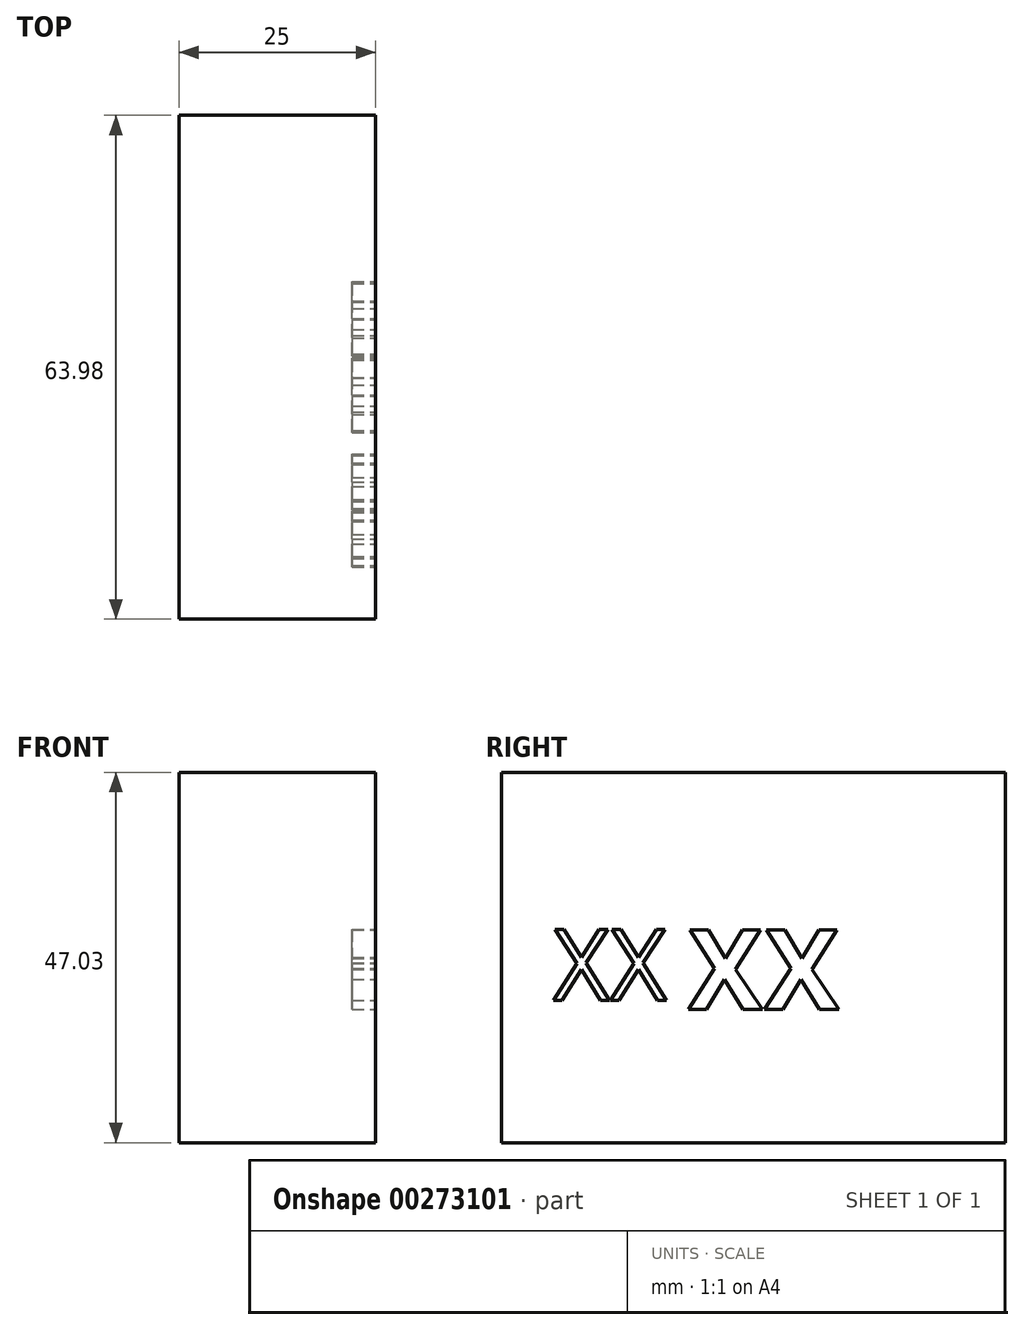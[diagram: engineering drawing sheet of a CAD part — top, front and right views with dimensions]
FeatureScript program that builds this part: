
annotation { "Feature Type Name" : "Feature", "Feature Type Description" : "" }
export const myFeature = defineFeature(function(context is Context, id is Id, definition is map)
    precondition{}
    {
        {
            var Q0;
            Q0=qCreatedBy(makeId("Right.planeOp"),FACE);
            var sketch = newSketch(context, id + "F0", { "sketchPlane" : qUnion([Q0])});
            skLineSegment(sketch, "E0.bottom", {"start": v(-63.98, 47.03) * mm, "end": v(0, 47.03) * mm});
            skLineSegment(sketch, "E0.top", {"start": v(-63.98, 0) * mm, "end": v(0, 0) * mm});
            skLineSegment(sketch, "E0.left", {"start": v(-63.98, 47.03) * mm, "end": v(-63.98, 0) * mm});
            skLineSegment(sketch, "E0.right", {"start": v(0, 47.03) * mm, "end": v(0, 0) * mm});
            skSolve(sketch);
        }
        {
            var Q0;
            Q0=makeQuery(id+"F0.imprint","IMPRINT",FACE,{"disambiguationData":[TD([[makeQuery(id+"F0.imprint","IMPRINT",EDGE,{"derivedFrom":sQuery(id+"F0.wireOp",EDGE,"E0.bottom")}),-1.0]])]});
            extrude(context, id + "F1", {"entities" : qUnion([Q0]), "depth" : 25 * mm});
        }
        {
            var Q0;
            Q0=makeQuery(id+"F1.opExtrude","CAP_FACE",FACE,{"disambiguationData":[OSD([sQuery(id+"F0.wireOp",EDGE,"E0.bottom"),sQuery(id+"F0.wireOp",EDGE,"E0.top"),sQuery(id+"F0.wireOp",EDGE,"E0.left"),sQuery(id+"F0.wireOp",EDGE,"E0.right")])],"isStart":false});
            var sketch = newSketch(context, id + "F2", { "sketchPlane" : qUnion([Q0])});
            skText(sketch, "E1", { "text": "XX", "fontName": "OpenSans-Regular.ttf"});
            const initialGuessF2  = {"E1": [-0.05746, 0.0181, 1, 0, 0.00904]};
            skSetInitialGuess(sketch, initialGuessF2);
            skSolve(sketch);
        }
        {
            var Q0;
            Q0 = qSketchRegion(id + "F2", true);
            extrude(context, id + "F3", {"entities" : qUnion([Q0]), "operationType" : NewBodyOperationType.REMOVE, "oppositeDirection" : true, "depth" : 3 * mm});
        }
        {
            var Q0;
            Q0=makeQuery(id+"F1.opExtrude","CAP_FACE",FACE,{"disambiguationData":[OSD([sQuery(id+"F0.wireOp",EDGE,"E0.bottom"),sQuery(id+"F0.wireOp",EDGE,"E0.top"),sQuery(id+"F0.wireOp",EDGE,"E0.left"),sQuery(id+"F0.wireOp",EDGE,"E0.right")])],"isStart":false});
            var sketch = newSketch(context, id + "F4", { "sketchPlane" : qUnion([Q0])});
            skText(sketch, "E2", { "text": "XX", "fontName": "OpenSans-Bold.ttf"});
            const initialGuessF4  = {"E2": [-0.04028, 0.01693, 1, 0, 0.01016]};
            skSetInitialGuess(sketch, initialGuessF4);
            skSolve(sketch);
        }
        {
            var Q0;
            Q0 = qSketchRegion(id + "F4", true);
            extrude(context, id + "F5", {"entities" : qUnion([Q0]), "operationType" : NewBodyOperationType.REMOVE, "oppositeDirection" : true, "depth" : 3 * mm});
        }
    });
